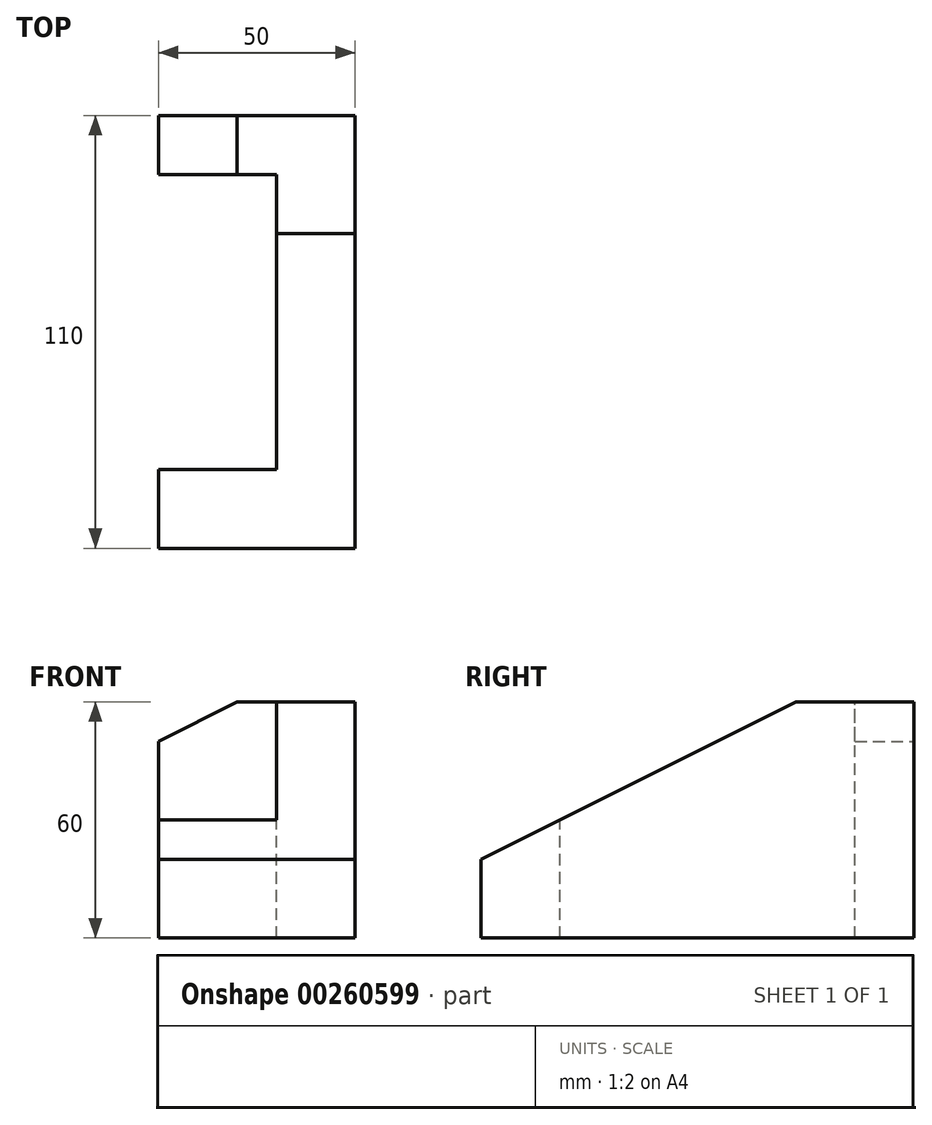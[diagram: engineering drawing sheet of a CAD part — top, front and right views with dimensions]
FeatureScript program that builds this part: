
annotation { "Feature Type Name" : "Feature", "Feature Type Description" : "" }
export const myFeature = defineFeature(function(context is Context, id is Id, definition is map)
    precondition{}
    {
        {
            assignVariable(context, id + "F0", {"name" : "B", "anyValue" : 60});
        }
        {
            var Q0;
            Q0=qCreatedBy(makeId("Top.planeOp"),FACE);
            var sketch = newSketch(context, id + "F1", { "sketchPlane" : qUnion([Q0])});
            skLineSegment(sketch, "E0.bottom", {"start": v(25, -55) * mm, "end": v(-25, -55) * mm});
            skLineSegment(sketch, "E0.top", {"start": v(25, 55) * mm, "end": v(-25, 55) * mm});
            skLineSegment(sketch, "E0.left", {"start": v(25, -55) * mm, "end": v(25, 55) * mm});
            skLineSegment(sketch, "E0.right", {"start": v(-25, -55) * mm, "end": v(-25, 55) * mm});
            skPoint(sketch, "E0.middle", {"position": v(0, 0) * mm});
            skSolve(sketch);
        }
        {
            var Q0;
            Q0=makeQuery(id+"F1.imprint","IMPRINT",FACE,{"disambiguationData":[TD([[makeQuery(id+"F1.imprint","IMPRINT",EDGE,{"derivedFrom":sQuery(id+"F1.wireOp",EDGE,"E0.bottom")}),-1.0]])]});
            extrude(context, id + "F2", {"entities" : qUnion([Q0]), "depth" : (getVariable(context, 'B')) * mm});
        }
        {
            var Q0;
            Q0=makeQuery(id+"F2.opExtrude","CAP_FACE",FACE,{"disambiguationData":[OSD([sQuery(id+"F1.wireOp",EDGE,"E0.bottom"),sQuery(id+"F1.wireOp",EDGE,"E0.top"),sQuery(id+"F1.wireOp",EDGE,"E0.left"),sQuery(id+"F1.wireOp",EDGE,"E0.right")])],"isStart":false});
            var sketch = newSketch(context, id + "F3", { "sketchPlane" : qUnion([Q0])});
            skLineSegment(sketch, "E1", {"start": v(-25, 40) * mm, "end": v(-25, -35) * mm});
            skLineSegment(sketch, "E2", {"start": v(-25, 40) * mm, "end": v(5, 40) * mm});
            skLineSegment(sketch, "E3", {"start": v(-25, -35) * mm, "end": v(5, -35) * mm});
            skLineSegment(sketch, "E4", {"start": v(5, -35) * mm, "end": v(5, 40) * mm});
            skSolve(sketch);
        }
        {
            var Q0;
            Q0=makeQuery(id+"F3.imprint","IMPRINT",FACE,{"disambiguationData":[TD([[makeQuery(id+"F3.imprint","IMPRINT",EDGE,{"derivedFrom":sQuery(id+"F3.wireOp",EDGE,"E1")}),-1.0]])]});
            extrude(context, id + "F4", {"entities" : qUnion([Q0]), "operationType" : NewBodyOperationType.REMOVE, "oppositeDirection" : true, "depth" : 60 * mm});
        }
        {
            var Q0;
            Q0=makeQuery(id+"F2.opExtrude","SWEPT_FACE",FACE,{"disambiguationData":[OSD([sQuery(id+"F1.wireOp",EDGE,"E0.top")])]});
            var sketch = newSketch(context, id + "F5", { "sketchPlane" : qUnion([Q0])});
            skLineSegment(sketch, "E5", {"start": v(25, 50) * mm, "end": v(5, 60) * mm});
            skLineSegment(sketch, "E6", {"start": v(5, 60) * mm, "end": v(25, 60) * mm});
            skLineSegment(sketch, "E7", {"start": v(25, 60) * mm, "end": v(25, 50) * mm});
            skSolve(sketch);
        }
        {
            var Q0;
            Q0=makeQuery(id+"F5.imprint","IMPRINT",FACE,{"disambiguationData":[TD([[makeQuery(id+"F5.imprint","IMPRINT",EDGE,{"derivedFrom":sQuery(id+"F5.wireOp",EDGE,"E5")}),-1.0]])]});
            extrude(context, id + "F6", {"entities" : qUnion([Q0]), "operationType" : NewBodyOperationType.REMOVE, "oppositeDirection" : true, "depth" : 15 * mm});
        }
        {
            var Q0;
            Q0=makeQuery(id+"F2.opExtrude","SWEPT_FACE",FACE,{"disambiguationData":[OSD([sQuery(id+"F1.wireOp",EDGE,"E0.left")])]});
            var sketch = newSketch(context, id + "F7", { "sketchPlane" : qUnion([Q0])});
            skLineSegment(sketch, "E8", {"start": v(25, 60) * mm, "end": v(-55, 20) * mm});
            skLineSegment(sketch, "E9", {"start": v(-55, 20) * mm, "end": v(-55, 60) * mm});
            skLineSegment(sketch, "E10", {"start": v(-55, 60) * mm, "end": v(25, 60) * mm});
            skSolve(sketch);
        }
        {
            var Q0;
            Q0=makeQuery(id+"F7.imprint","IMPRINT",FACE,{"disambiguationData":[TD([[makeQuery(id+"F7.imprint","IMPRINT",EDGE,{"derivedFrom":sQuery(id+"F7.wireOp",EDGE,"E8")}),-1.0]])]});
            extrude(context, id + "F8", {"entities" : qUnion([Q0]), "operationType" : NewBodyOperationType.REMOVE, "oppositeDirection" : true, "depth" : 50 * mm});
        }
    });
